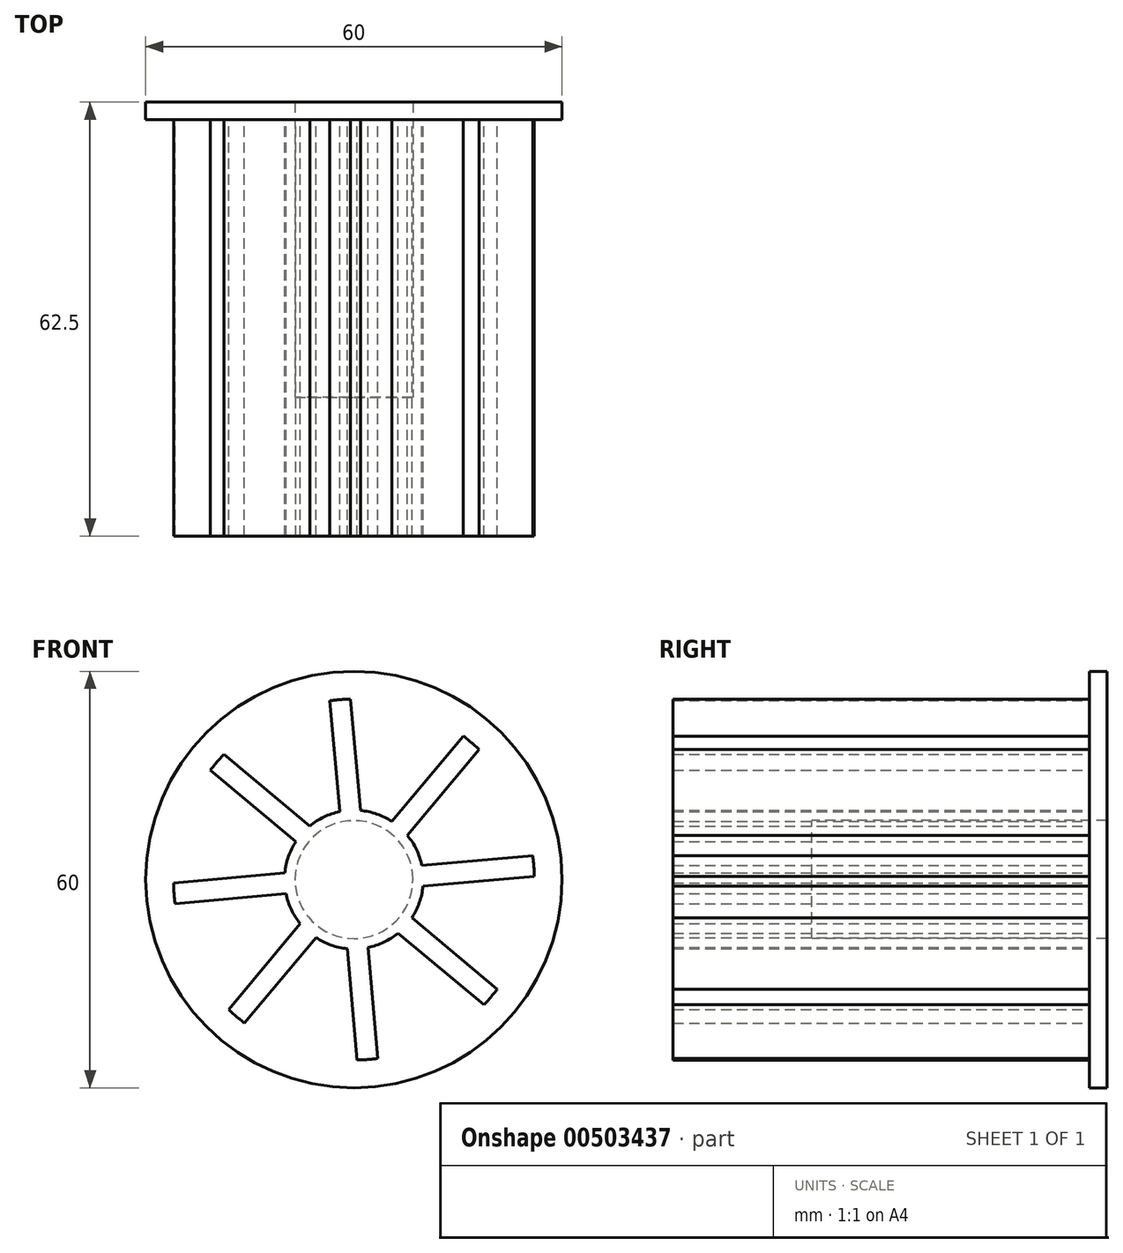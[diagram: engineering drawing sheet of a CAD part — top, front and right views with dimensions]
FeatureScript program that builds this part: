
annotation { "Feature Type Name" : "Feature", "Feature Type Description" : "" }
export const myFeature = defineFeature(function(context is Context, id is Id, definition is map)
    precondition{}
    {
        {
            var Q0;
            Q0=qCreatedBy(makeId("Front.planeOp"),FACE);
            var sketch = newSketch(context, id + "F0", { "sketchPlane" : qUnion([Q0])});
            skCircle(sketch, "E0", {"center": v(0, 0) * mm, "radius": 30 * mm});
            skCircle(sketch, "E1", {"center": v(0, 0) * mm, "radius": 8.5 * mm});
            skSolve(sketch);
        }
        {
            var Q0;
            Q0=qSketchRegion(id+"F0",true);
            extrude(context, id + "F1", {"entities" : qUnion([Q0]), "oppositeDirection" : true, "depth" : 2.5 * mm});
        }
        {
            var Q0;
            Q0=qCreatedBy(makeId("Front.planeOp"),FACE);
            var sketch = newSketch(context, id + "F2", { "sketchPlane" : qUnion([Q0])});
            skCircle(sketch, "E2", {"center": v(0, 0) * mm, "radius": 10 * mm});
            skArc(sketch, "E3", {"start": v(18.71, -18.05) * mm, "mid": v(19.72, -16.94) * mm, "end": v(20.67, -15.77) * mm});
            skLineSegment(sketch, "E4", {"start": v(18.71, -18.05) * mm, "end": v(6.36, -7.72) * mm});
            skLineSegment(sketch, "E5", {"start": v(20.67, -15.77) * mm, "end": v(8.36, -5.48) * mm});
            skLineSegment(sketch, "E6.1.0", {"start": v(25.77, 3.46) * mm, "end": v(9.8, 2.04) * mm});
            skLineSegment(sketch, "E6.1.1", {"start": v(26, 0.47) * mm, "end": v(9.95, -0.96) * mm});
            skArc(sketch, "E6.1.2", {"start": v(26, 0.47) * mm, "mid": v(25.93, 1.97) * mm, "end": v(25.77, 3.46) * mm});
            skLineSegment(sketch, "E6.2.0", {"start": v(15.77, 20.67) * mm, "end": v(5.48, 8.36) * mm});
            skLineSegment(sketch, "E6.2.1", {"start": v(18.05, 18.71) * mm, "end": v(7.72, 6.36) * mm});
            skArc(sketch, "E6.2.2", {"start": v(18.05, 18.71) * mm, "mid": v(16.94, 19.72) * mm, "end": v(15.77, 20.67) * mm});
            skLineSegment(sketch, "E6.3.0", {"start": v(-3.46, 25.77) * mm, "end": v(-2.04, 9.8) * mm});
            skLineSegment(sketch, "E6.3.1", {"start": v(-0.47, 26) * mm, "end": v(0.96, 9.95) * mm});
            skArc(sketch, "E6.3.2", {"start": v(-0.47, 26) * mm, "mid": v(-1.97, 25.93) * mm, "end": v(-3.46, 25.77) * mm});
            skLineSegment(sketch, "E6.4.0", {"start": v(-20.67, 15.77) * mm, "end": v(-8.36, 5.48) * mm});
            skLineSegment(sketch, "E6.4.1", {"start": v(-18.71, 18.05) * mm, "end": v(-6.36, 7.72) * mm});
            skArc(sketch, "E6.4.2", {"start": v(-18.71, 18.05) * mm, "mid": v(-19.72, 16.94) * mm, "end": v(-20.67, 15.77) * mm});
            skLineSegment(sketch, "E6.5.0", {"start": v(-25.77, -3.46) * mm, "end": v(-9.8, -2.04) * mm});
            skLineSegment(sketch, "E6.5.1", {"start": v(-26, -0.47) * mm, "end": v(-9.95, 0.96) * mm});
            skArc(sketch, "E6.5.2", {"start": v(-26, -0.47) * mm, "mid": v(-25.93, -1.97) * mm, "end": v(-25.77, -3.46) * mm});
            skLineSegment(sketch, "E6.6.0", {"start": v(-15.77, -20.67) * mm, "end": v(-5.48, -8.36) * mm});
            skLineSegment(sketch, "E6.6.1", {"start": v(-18.05, -18.71) * mm, "end": v(-7.72, -6.36) * mm});
            skArc(sketch, "E6.6.2", {"start": v(-18.05, -18.71) * mm, "mid": v(-16.94, -19.72) * mm, "end": v(-15.77, -20.67) * mm});
            skLineSegment(sketch, "E6.7.0", {"start": v(3.46, -25.77) * mm, "end": v(2.04, -9.8) * mm});
            skLineSegment(sketch, "E6.7.1", {"start": v(0.47, -26) * mm, "end": v(-0.96, -9.95) * mm});
            skArc(sketch, "E6.7.2", {"start": v(0.47, -26) * mm, "mid": v(1.97, -25.93) * mm, "end": v(3.46, -25.77) * mm});
            skSolve(sketch);
        }
        {
            var Q0;
            {var subQ0=sQuery(id+"F2.wireOp",EDGE,"E2");var subQ8=makeQuery(id+"F2.imprint","INTERSECT",VERTEX,{"derivedFrom":[subQ0,sQuery(id+"F2.wireOp",EDGE,"E6.1.0")]});Q0=makeQuery(id+"F2.imprint","IMPRINT",FACE,{"disambiguationData":[TD([[makeQuery(id+"F2.imprint","IMPRINT",EDGE,{"disambiguationData":[TD([[subQ8,-1.0]])],"derivedFrom":subQ0}),1.0]])]});}
            var Q1;
            {var subQ0=sQuery(id+"F2.wireOp",EDGE,"E6.4.0");Q1=makeQuery(id+"F2.imprint","IMPRINT",FACE,{"disambiguationData":[TD([[makeQuery(id+"F2.imprint","IMPRINT",EDGE,{"derivedFrom":subQ0}),1.0]])]});}
            var Q2;
            {var subQ0=sQuery(id+"F2.wireOp",EDGE,"E6.6.0");Q2=makeQuery(id+"F2.imprint","IMPRINT",FACE,{"disambiguationData":[TD([[makeQuery(id+"F2.imprint","IMPRINT",EDGE,{"derivedFrom":subQ0}),1.0]])]});}
            var Q3;
            {var subQ0=sQuery(id+"F2.wireOp",EDGE,"E6.7.0");Q3=makeQuery(id+"F2.imprint","IMPRINT",FACE,{"disambiguationData":[TD([[makeQuery(id+"F2.imprint","IMPRINT",EDGE,{"derivedFrom":subQ0}),1.0]])]});}
            var Q4;
            Q4=makeQuery(id+"F2.imprint","IMPRINT",FACE,{"disambiguationData":[TD([[makeQuery(id+"F2.imprint","IMPRINT",EDGE,{"derivedFrom":sQuery(id+"F2.wireOp",EDGE,"E3")}),1.0]])]});
            var Q5;
            {var subQ0=sQuery(id+"F2.wireOp",EDGE,"E6.1.0");Q5=makeQuery(id+"F2.imprint","IMPRINT",FACE,{"disambiguationData":[TD([[makeQuery(id+"F2.imprint","IMPRINT",EDGE,{"derivedFrom":subQ0}),1.0]])]});}
            var Q6;
            {var subQ0=sQuery(id+"F2.wireOp",EDGE,"E6.2.0");Q6=makeQuery(id+"F2.imprint","IMPRINT",FACE,{"disambiguationData":[TD([[makeQuery(id+"F2.imprint","IMPRINT",EDGE,{"derivedFrom":subQ0}),1.0]])]});}
            var Q7;
            {var subQ0=sQuery(id+"F2.wireOp",EDGE,"E6.3.0");Q7=makeQuery(id+"F2.imprint","IMPRINT",FACE,{"disambiguationData":[TD([[makeQuery(id+"F2.imprint","IMPRINT",EDGE,{"derivedFrom":subQ0}),1.0]])]});}
            var Q8;
            {var subQ0=sQuery(id+"F2.wireOp",EDGE,"E6.5.0");Q8=makeQuery(id+"F2.imprint","IMPRINT",FACE,{"disambiguationData":[TD([[makeQuery(id+"F2.imprint","IMPRINT",EDGE,{"derivedFrom":subQ0}),1.0]])]});}
            extrude(context, id + "F3", {"entities" : qUnion([Q0, Q1, Q2, Q3, Q4, Q5, Q6, Q7, Q8]), "operationType" : NewBodyOperationType.ADD, "depth" : 60 * mm, "offsetDistance" : 25 * mm});
        }
        {
            var Q0;
            Q0=makeQuery(id+"F3.opExtrude","CAP_FACE",FACE,{"disambiguationData":[OSD([sQuery(id+"F2.wireOp",EDGE,"E2"),sQuery(id+"F2.wireOp",EDGE,"E3"),sQuery(id+"F2.wireOp",EDGE,"E4"),sQuery(id+"F2.wireOp",EDGE,"E5"),sQuery(id+"F2.wireOp",EDGE,"E6.1.0"),sQuery(id+"F2.wireOp",EDGE,"E6.1.1"),sQuery(id+"F2.wireOp",EDGE,"E6.1.2"),sQuery(id+"F2.wireOp",EDGE,"E6.2.0"),sQuery(id+"F2.wireOp",EDGE,"E6.2.1"),sQuery(id+"F2.wireOp",EDGE,"E6.2.2"),sQuery(id+"F2.wireOp",EDGE,"E6.3.0"),sQuery(id+"F2.wireOp",EDGE,"E6.3.1"),sQuery(id+"F2.wireOp",EDGE,"E6.3.2"),sQuery(id+"F2.wireOp",EDGE,"E6.4.0"),sQuery(id+"F2.wireOp",EDGE,"E6.4.1"),sQuery(id+"F2.wireOp",EDGE,"E6.4.2"),sQuery(id+"F2.wireOp",EDGE,"E6.5.0"),sQuery(id+"F2.wireOp",EDGE,"E6.5.1"),sQuery(id+"F2.wireOp",EDGE,"E6.5.2"),sQuery(id+"F2.wireOp",EDGE,"E6.6.0"),sQuery(id+"F2.wireOp",EDGE,"E6.6.1"),sQuery(id+"F2.wireOp",EDGE,"E6.6.2"),sQuery(id+"F2.wireOp",EDGE,"E6.7.0"),sQuery(id+"F2.wireOp",EDGE,"E6.7.1"),sQuery(id+"F2.wireOp",EDGE,"E6.7.2")])],"isStart":true});
            extrude(context, id + "F4", {"entities" : qUnion([Q0]), "operationType" : NewBodyOperationType.REMOVE, "oppositeDirection" : true, "depth" : 40 * mm});
        }
    });
